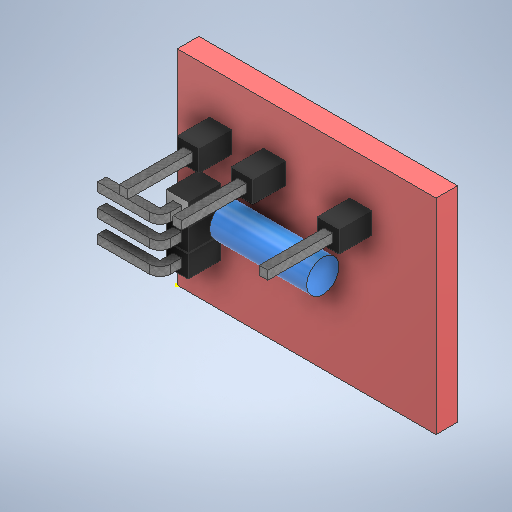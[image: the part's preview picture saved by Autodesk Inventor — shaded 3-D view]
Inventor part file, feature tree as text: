
AUTODESK INVENTOR PART (.ipt)
format: ipt  version: 2025.1 (Build 291241020, 241B)  size: 478,208 bytes
history: native  units: in
note: dims shown in document units (in); Inventor stores cm internally (conversion verified against a paired STEP export)
features: projected_geometry x13, sketch x8, extrude x6, plane x1, fillet x1
ambient origin geometry x8: Origin, YZ Plane, XZ Plane, XY Plane, X Axis, Y Axis, Z Axis, Center Point
bodies: Solid1 (feature_tree)
feature tree (29):
  extrude  "Extrusion1"  Depth=0.748in
  plane  "Work Plane1"
  extrude  "Extrusion2"  [1 undecoded]
  sketch  "Sketch3"  dims[d5=0.1181in d6=0.3543in]
  extrude  "Extrusion3"  Depth=0.3543in
  extrude  "Extrusion4"  Depth=0.0787in
  extrude  "Extrusion5"  Depth=0.0787in
  extrude  "Extrusion6"  Depth=0.0787in
  fillet  "Fillet1"  Radius=0.0787in
  sketch  "Sketch8"  dims[d21=0.2362in d22=0.5512in d23=0.748in d24=0.1575in d25=0.1575in d26=0.0039in d27=0.0039in d28=0.0787in d29=0.1181in d30=0.0in d31=0.0315in d32=0.0315in d33=0.0315in d34=0.0315in d35=0.0315in d36=0.0315in d37=0.0315in d38=0.0315in d39=0.0315in d40=0.0315in d41=0.0315in d42=0.0315in d43=0.2362in d44=0.0in d45=0.0315in d46=0.0315in d47=0.0315in d48=0.0315in d49=0.0315in d50=0.0315in d51=0.0787in d52=0.0in d53=0.0315in d54=0.0315in d55=0.0315in d56=0.1969in d57=0.0in d58=0.0394in d59=0.0945in]
  sketch  "Sketch1"  dims[d0=0.9449in d1=0.748in]
  sketch  "Sketch2"  dims[d2=0.0787in d3=0.0in d4=-0.3543in]
  sketch  "Sketch4"  dims[d7=0.3543in d8=0.0in d9=0.0787in]
  sketch  "Sketch5"  dims[d10=0.0787in d11=0.0787in d12=0.0787in]
  projected_geometry  "Projected Loop1"
  projected_geometry  "Projected Loop2"
  projected_geometry  "Projected Loop3"
  projected_geometry  "Projected Loop4"
  projected_geometry  "Projected Loop5"
  projected_geometry  "Projected Loop6"
  sketch  "Sketch6"  dims[d13=0.0787in d14=0.0787in d15=0.0787in d16=0.0787in d17=0.0787in d18=0.0787in]
  projected_geometry  "Projected Loop7"
  projected_geometry  "Projected Loop8"
  projected_geometry  "Projected Loop9"
  sketch  "Sketch7"  dims[d19=0.0787in d20=0.0787in]
  projected_geometry  "Projected Loop10"
  projected_geometry  "Projected Loop11"
  projected_geometry  "Projected Loop12"
  projected_geometry  "Projected Loop13"
note: 1 required parameter value undecoded (feature->parameter linkage not recoverable at this tier; creation-order binding heuristic only, values carry confidence <= 0.55)
